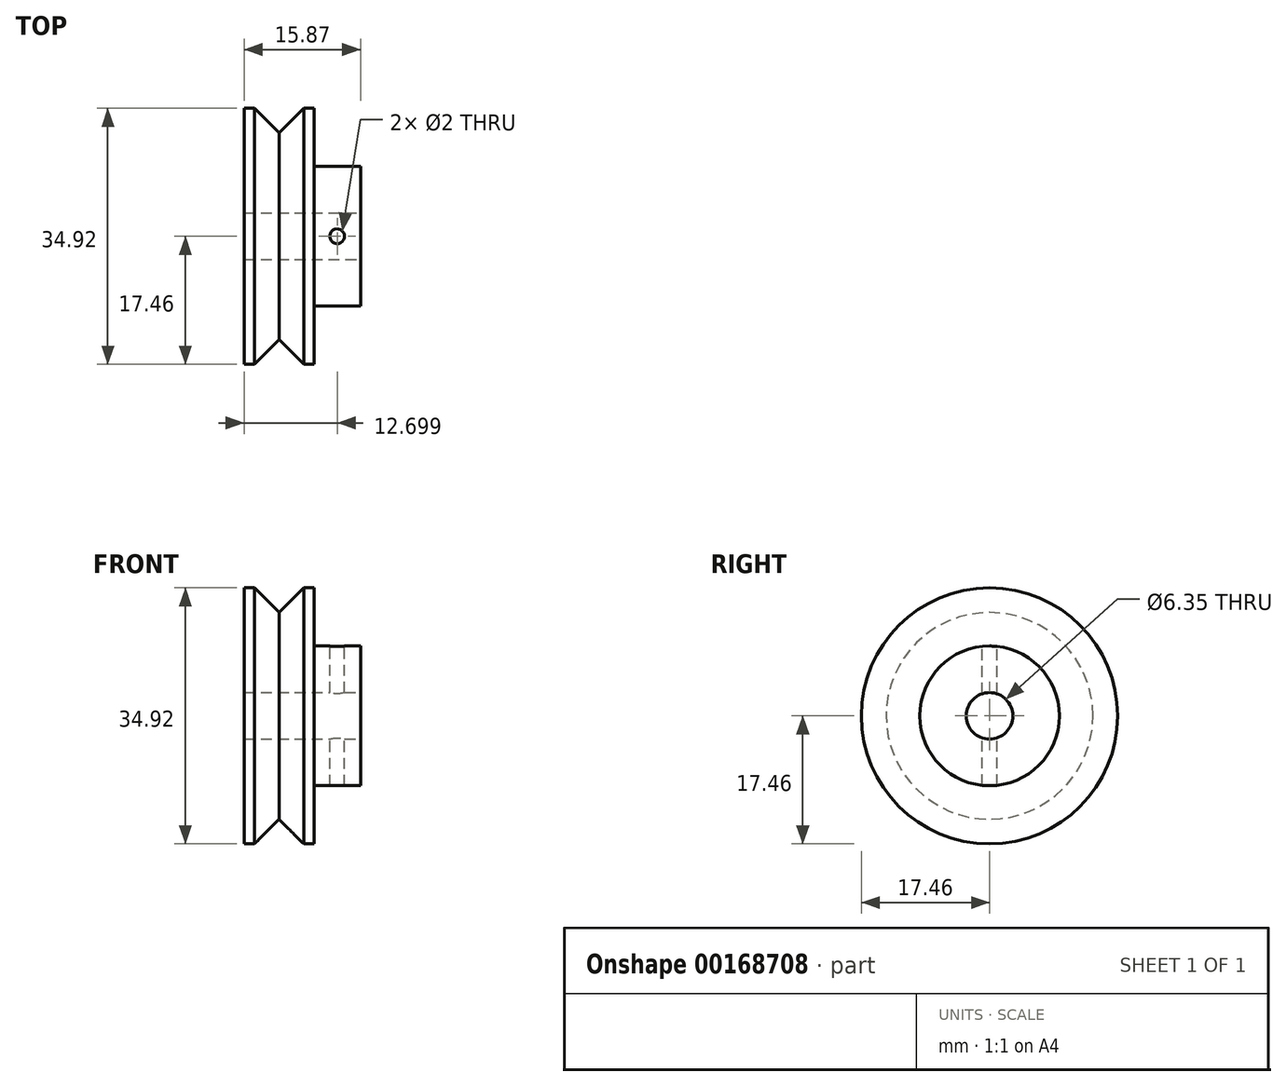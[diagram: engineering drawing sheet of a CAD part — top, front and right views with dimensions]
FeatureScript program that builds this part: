
annotation { "Feature Type Name" : "Feature", "Feature Type Description" : "" }
export const myFeature = defineFeature(function(context is Context, id is Id, definition is map)
    precondition{}
    {
        {
            var Q0;
            Q0=qCreatedBy(makeId("Front.planeOp"),FACE);
            var sketch = newSketch(context, id + "F0", { "sketchPlane" : qUnion([Q0])});
            skLineSegment(sketch, "E0", {"start": v(13.74, 3.18) * mm, "end": v(13.74, 9.53) * mm});
            skLineSegment(sketch, "E1", {"start": v(13.74, 9.53) * mm, "end": v(7.4, 9.53) * mm});
            skLineSegment(sketch, "E2", {"start": v(7.4, 9.53) * mm, "end": v(7.4, 17.46) * mm});
            skLineSegment(sketch, "E3", {"start": v(7.4, 17.46) * mm, "end": v(-2.13, 17.46) * mm});
            skLineSegment(sketch, "E4", {"start": v(-2.13, 17.46) * mm, "end": v(-2.13, 3.18) * mm});
            skLineSegment(sketch, "E5", {"start": v(-2.13, 3.18) * mm, "end": v(13.74, 3.18) * mm});
            skLineSegment(sketch, "E6", {"start": v(4.12, 0) * mm, "end": v(-4.41, 0) * mm, "construction": true});
            skSolve(sketch);
        }
        {
            var Q0;
            Q0=qSketchRegion(id+"F0",true);
            var Q1;
            Q1=sQuery(id+"F0.wireOp",EDGE,"E6");
            revolve(context, id + "F1", {"entities" : qUnion([Q0]), "axis" : qUnion([Q1]), "revolveType" : RevolveType.FULL});
        }
        {
            var Q0;
            Q0=qCreatedBy(makeId("Top.planeOp"),FACE);
            cPlane(context, id + "F2", {"entities" : qUnion([Q0]), "cplaneType" : CPlaneType.OFFSET, "offset" : 9.55 * mm, "width" : 150 * mm, "height" : 150 * mm});
        }
        {
            var Q0;
            Q0=qCreatedBy(id+"F2.planeOp",FACE);
            var sketch = newSketch(context, id + "F3", { "sketchPlane" : qUnion([Q0])});
            skCircle(sketch, "E7", {"center": v(10.57, 0) * mm, "radius": 1 * mm});
            skLineSegment(sketch, "E8.0", {"start": v(7.4, 17.46) * mm, "end": v(7.4, -17.46) * mm, "construction": true});
            skLineSegment(sketch, "E9", {"start": v(7.4, 0) * mm, "end": v(13.74, 0) * mm});
            skLineSegment(sketch, "E10.0", {"start": v(13.74, 9.53) * mm, "end": v(13.74, -9.53) * mm, "construction": true});
            skSolve(sketch);
        }
        {
            var Q0;
            Q0=qSketchRegion(id+"F3",true);
            extrude(context, id + "F4", {"entities" : qUnion([Q0]), "operationType" : NewBodyOperationType.REMOVE, "endBound" : BoundingType.THROUGH_ALL, "oppositeDirection" : true, "depth" : 25 * mm});
        }
        {
            var Q0;
            Q0=qCreatedBy(id+"F2.planeOp",FACE);
            var sketch = newSketch(context, id + "F5", { "sketchPlane" : qUnion([Q0])});
            skLineSegment(sketch, "E11", {"start": v(-2.13, 17.46) * mm, "end": v(7.4, 17.46) * mm});
            skLineSegment(sketch, "E12.0", {"start": v(-2.13, 17.46) * mm, "end": v(-2.13, -17.46) * mm});
            skLineSegment(sketch, "E13.0", {"start": v(7.4, 17.46) * mm, "end": v(7.4, -17.46) * mm});
            skSolve(sketch);
        }
        {
            var Q0;
            Q0=qCreatedBy(makeId("Top.planeOp"),FACE);
            var sketch = newSketch(context, id + "F6", { "sketchPlane" : qUnion([Q0])});
            skLineSegment(sketch, "E14.0", {"start": v(-2.13, 17.46) * mm, "end": v(-2.13, -17.46) * mm});
            skLineSegment(sketch, "E15.0", {"start": v(-2.13, 17.46) * mm, "end": v(7.4, 17.46) * mm});
            skLineSegment(sketch, "E16.0", {"start": v(7.4, 17.46) * mm, "end": v(7.4, -17.46) * mm});
            skLineSegment(sketch, "E17", {"start": v(2.63, 17.46) * mm, "end": v(2.63, 9.64) * mm, "construction": true});
            skLineSegment(sketch, "E18", {"start": v(2.63, 14.1) * mm, "end": v(6, 17.46) * mm});
            skLineSegment(sketch, "E19", {"start": v(6, 17.46) * mm, "end": v(-0.73, 17.46) * mm});
            skLineSegment(sketch, "E20", {"start": v(-0.73, 17.46) * mm, "end": v(2.63, 14.1) * mm});
            skLineSegment(sketch, "E21", {"start": v(-2.13, 0) * mm, "end": v(13.75, 0) * mm, "construction": true});
            skPoint(sketch, "E21.endSnap0", {"position": v(-2.13, 0) * mm});
            skSolve(sketch);
        }
        {
            var Q0;
            Q0 = qSketchRegion(id + "F6", true);
            var Q1;
            Q1=sQuery(id+"F6.wireOp",EDGE,"E21");
            revolve(context, id + "F7", {"operationType" : NewBodyOperationType.REMOVE, "entities" : qUnion([Q0]), "axis" : qUnion([Q1]), "revolveType" : RevolveType.FULL, "oppositeDirection" : true});
        }
    });
